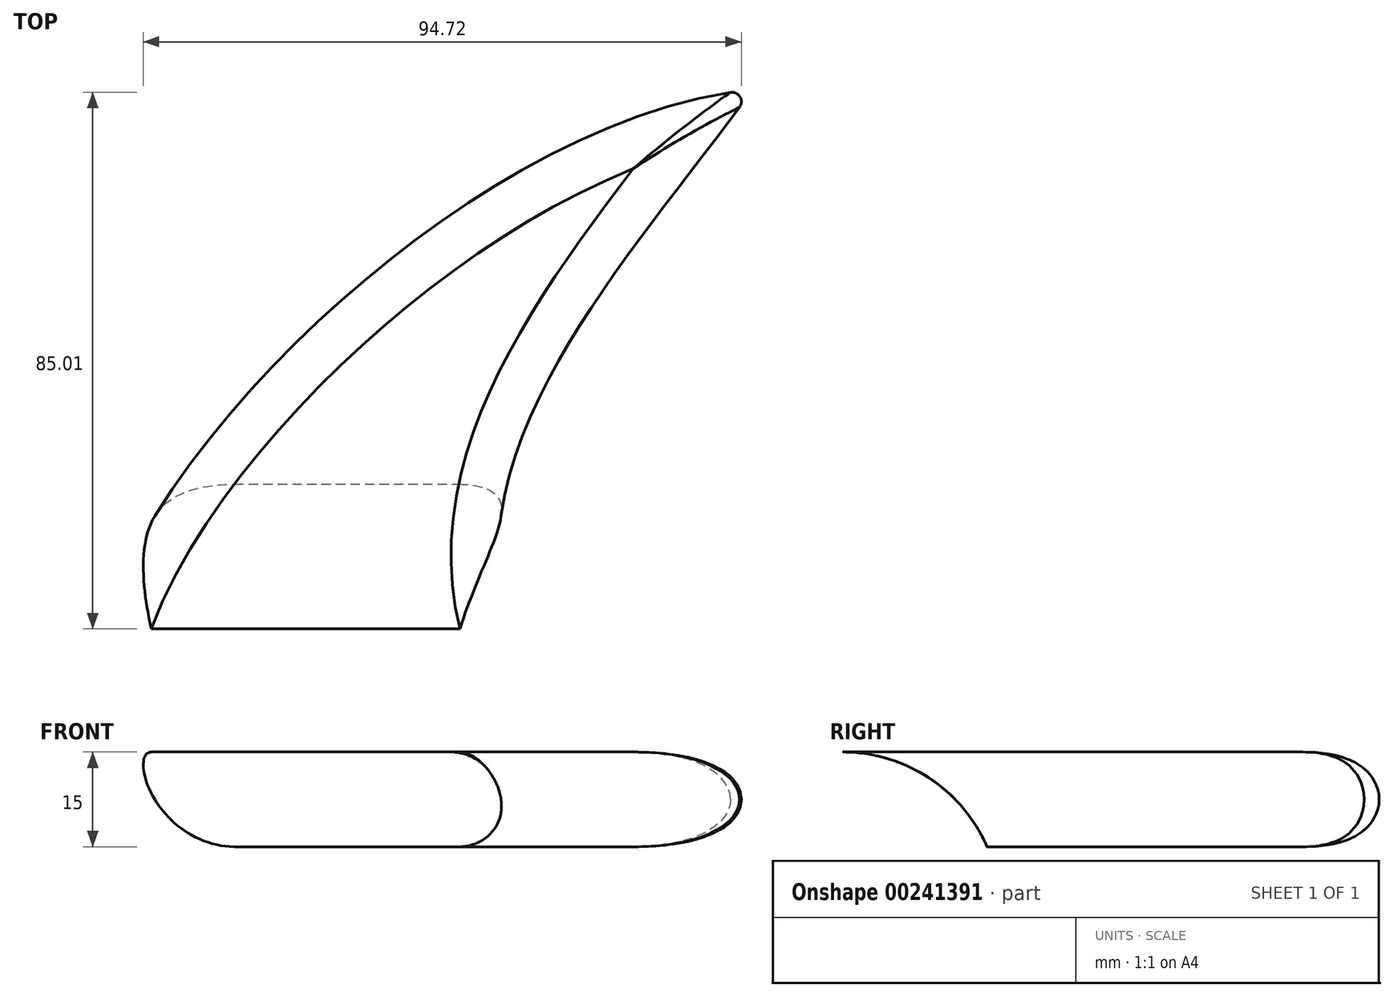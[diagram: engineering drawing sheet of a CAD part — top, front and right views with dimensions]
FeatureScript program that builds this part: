
annotation { "Feature Type Name" : "Feature", "Feature Type Description" : "" }
export const myFeature = defineFeature(function(context is Context, id is Id, definition is map)
    precondition{}
    {
        {
            var Q0;
            Q0=qCreatedBy(makeId("Top.planeOp"),FACE);
            var sketch = newSketch(context, id + "F0", { "sketchPlane" : qUnion([Q0])});
            skLineSegment(sketch, "E0", {"start": v(-26.94, 0) * mm, "end": v(37.6, 0) * mm});
            skPoint(sketch, "E1", {"position": v(76.2, 85.43) * mm});
            skFitSpline(sketch, "E2", {"points": [v(-26.94, 0) * mm, v(76.2, 85.43) * mm], "startDerivative": vector(30.2, 99.47) * mm, "endDerivative": vector(123.98, 11.95) * mm});
            skFitSpline(sketch, "E3", {"points": [v(37.6, 0) * mm, v(76.2, 85.43) * mm], "startDerivative": vector(-26.1, 89) * mm, "endDerivative": vector(61.24, 83.65) * mm});
            skSolve(sketch);
        }
        {
            var Q0;
            Q0=qSketchRegion(id+"F0",true);
            extrude(context, id + "F1", {"entities" : qUnion([Q0]), "depth" : 15 * mm});
        }
        {
            var Q0;
            Q0=makeQuery(id+"F1.opExtrude","SWEPT_EDGE",EDGE,{"disambiguationData":[OSD([sQuery(id+"F0.wireOp",EDGE,"E2"),sQuery(id+"F0.wireOp",EDGE,"E3")])]});
            fillet(context, id + "F2", {"entities" : qUnion([Q0]), "radius" : 1.5 * mm, "tangentPropagation" : true, "allowEdgeOverflow" : false});
        }
        {
            var Q0;
            Q0=makeQuery(id+"F1.opExtrude","CAP_EDGE",EDGE,{"disambiguationData":[OSD([sQuery(id+"F0.wireOp",EDGE,"E2")])],"isStart":false});
            var Q1;
            Q1=makeQuery(id+"F1.opExtrude","CAP_EDGE",EDGE,{"disambiguationData":[OSD([sQuery(id+"F0.wireOp",EDGE,"E2")])],"isStart":true});
            fillet(context, id + "F3", {"entities" : qUnion([Q0, Q1]), "radius" : 7.5 * mm, "tangentPropagation" : true, "allowEdgeOverflow" : false});
        }
        {
            var Q0;
            Q0=qCreatedBy(makeId("Right.planeOp"),FACE);
            var sketch = newSketch(context, id + "F4", { "sketchPlane" : qUnion([Q0])});
            skLineSegment(sketch, "E4.bottom", {"start": v(-186.4, -35) * mm, "end": v(25, -35) * mm});
            skLineSegment(sketch, "E4.top", {"start": v(-186.4, 15) * mm, "end": v(0, 15) * mm});
            skLineSegment(sketch, "E4.left", {"start": v(-186.4, -35) * mm, "end": v(-186.4, 15) * mm});
            skLineSegment(sketch, "E4.right", {"start": v(25, -35) * mm, "end": v(25, -10) * mm});
            skPoint(sketch, "E5.visualSharp", {"position": v(25, 15) * mm});
            skArc(sketch, "E5.filletArc", {"start": v(25, -10) * mm, "mid": v(17.68, 7.68) * mm, "end": v(0, 15) * mm});
            skSolve(sketch);
        }
        {
            var Q0;
            Q0=qSketchRegion(id+"F4",true);
            extrude(context, id + "F5", {"entities" : qUnion([Q0]), "operationType" : NewBodyOperationType.REMOVE, "endBound" : BoundingType.SYMMETRIC, "oppositeDirection" : true, "depth" : 100 * mm});
        }
    });
